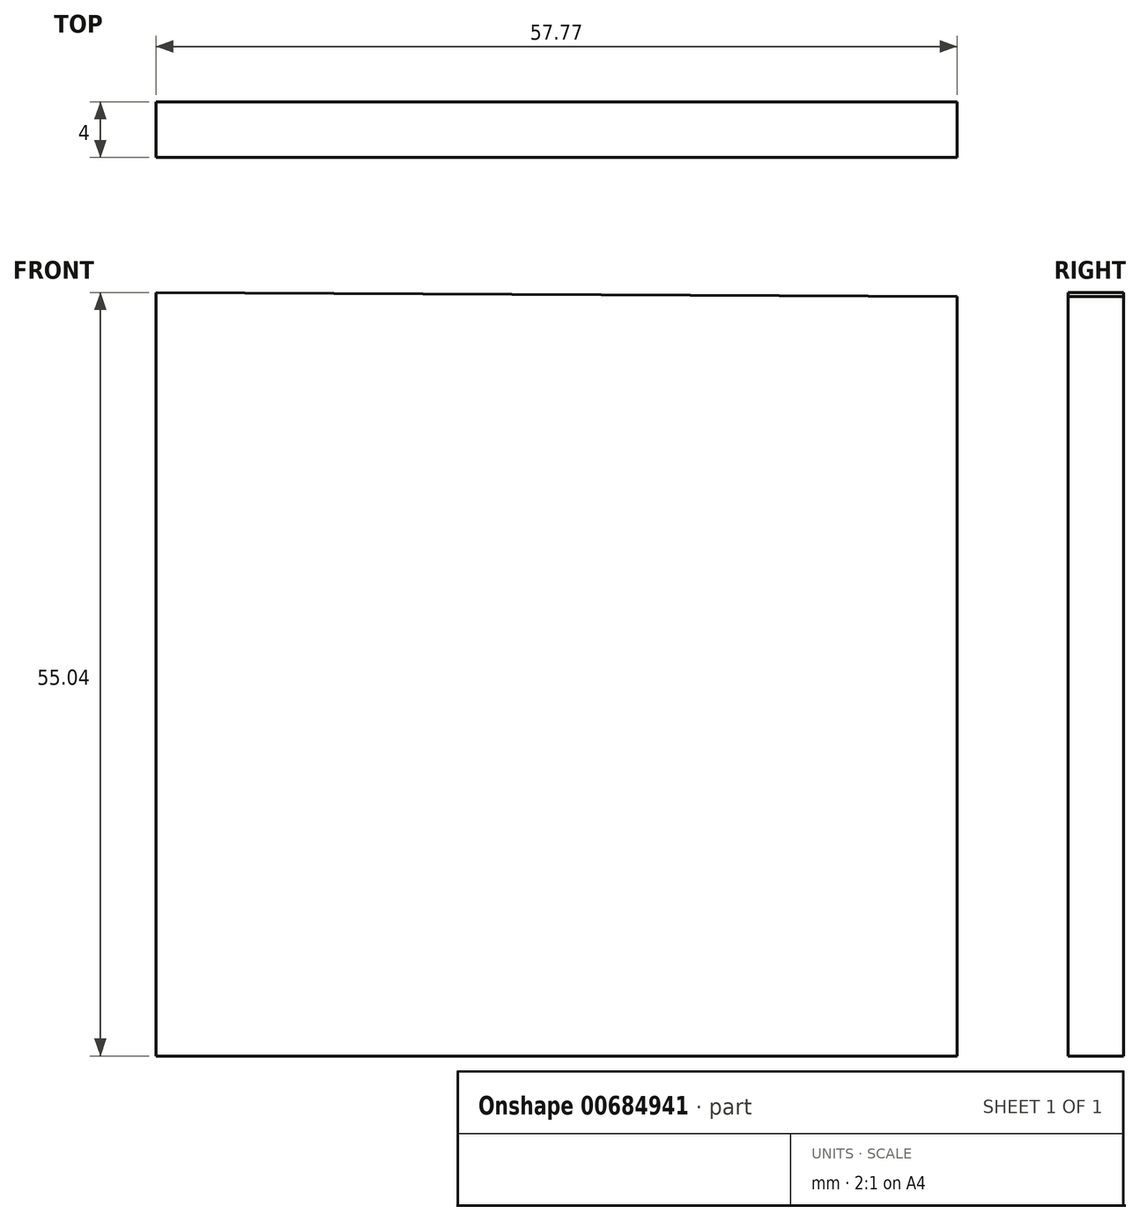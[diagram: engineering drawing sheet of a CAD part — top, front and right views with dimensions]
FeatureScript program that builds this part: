
annotation { "Feature Type Name" : "Feature", "Feature Type Description" : "" }
export const myFeature = defineFeature(function(context is Context, id is Id, definition is map)
    precondition{}
    {
        {
            var Q0;
            Q0=qCreatedBy(makeId("Front.planeOp"),FACE);
            var sketch = newSketch(context, id + "F0", { "sketchPlane" : qUnion([Q0])});
            skLineSegment(sketch, "E0", {"start": v(-28.6, 55.04) * mm, "end": v(-28.6, 0) * mm});
            skLineSegment(sketch, "E1", {"start": v(-28.6, 0) * mm, "end": v(29.17, 0) * mm});
            skLineSegment(sketch, "E2", {"start": v(29.17, 0) * mm, "end": v(29.17, 54.75) * mm});
            skLineSegment(sketch, "E3", {"start": v(29.17, 54.75) * mm, "end": v(-28.6, 55.04) * mm});
            skSolve(sketch);
        }
        {
            var Q0;
            Q0=makeQuery(id+"F0.imprint","IMPRINT",FACE,{"disambiguationData":[TD([[makeQuery(id+"F0.imprint","IMPRINT",EDGE,{"derivedFrom":sQuery(id+"F0.wireOp",EDGE,"E0")}),1.0]])]});
            extrude(context, id + "F1", {"entities" : qUnion([Q0]), "depth" : 4 * mm, "offsetDistance" : 25 * mm});
        }
    });
